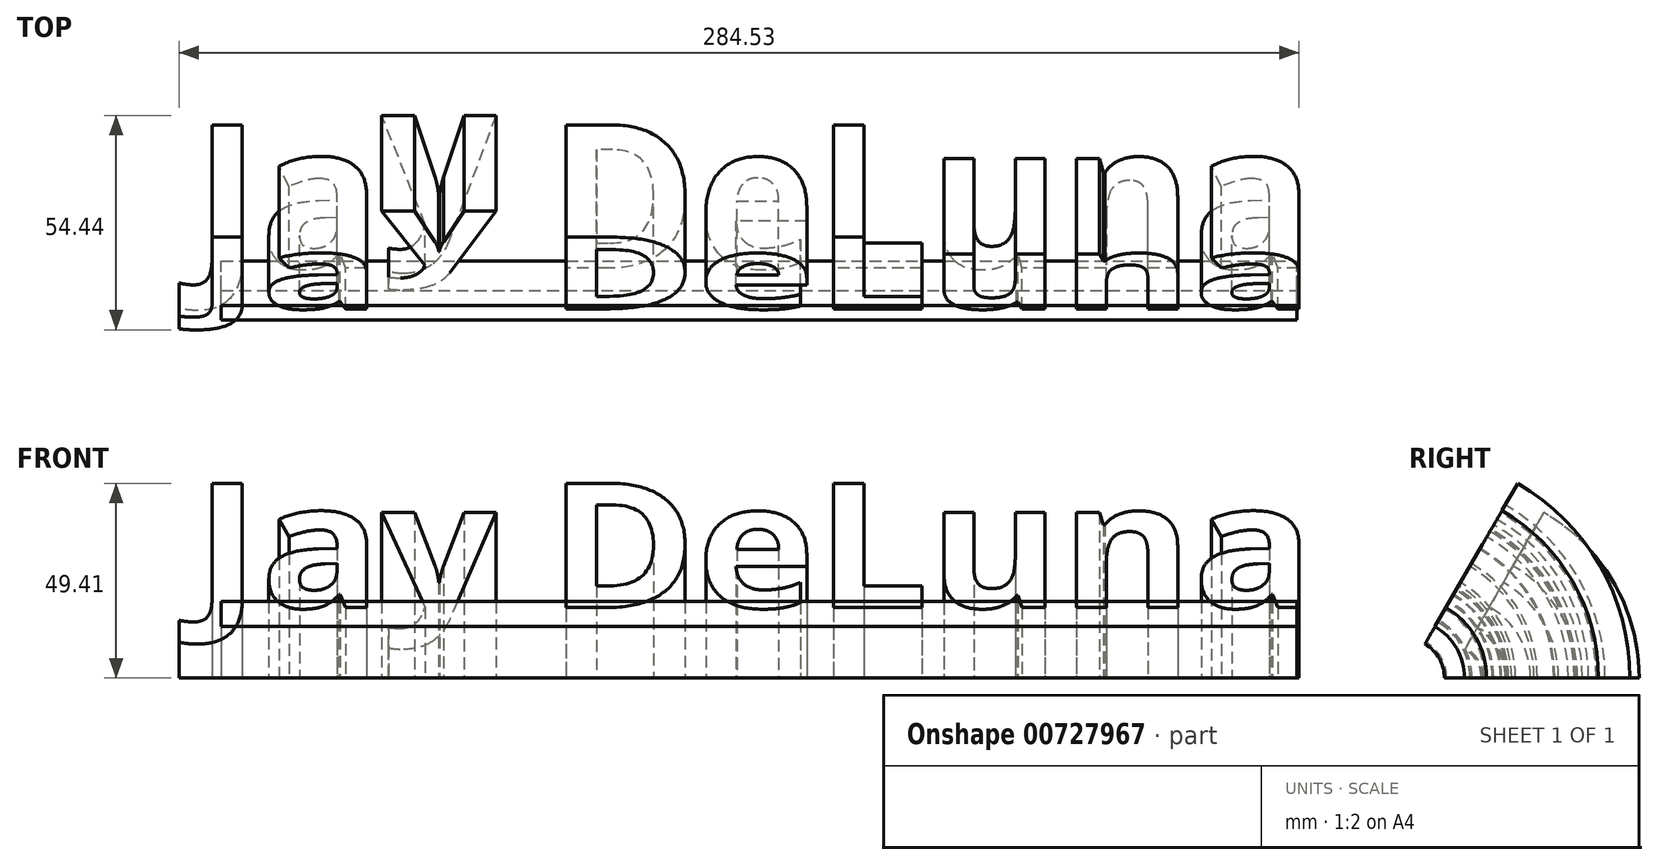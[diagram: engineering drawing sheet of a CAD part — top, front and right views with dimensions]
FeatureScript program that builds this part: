
annotation { "Feature Type Name" : "Feature", "Feature Type Description" : "" }
export const myFeature = defineFeature(function(context is Context, id is Id, definition is map)
    precondition{}
    {
        {
            var Q0;
            Q0=qCreatedBy(makeId("Top.planeOp"),FACE);
            var sketch = newSketch(context, id + "F0", { "sketchPlane" : qUnion([Q0])});
            skText(sketch, "E0", { "text": "Jay DeLuna", "fontName": "OpenSans-Bold.ttf"});
            const initialGuessF0  = {"E0": [-0.11567, -0.01428, 1, 0, 0.03673]};
            skSetInitialGuess(sketch, initialGuessF0);
            skSolve(sketch);
        }
        {
            var Q0;
            Q0=qCreatedBy(makeId("Top.planeOp"),FACE);
            var sketch = newSketch(context, id + "F1", { "sketchPlane" : qUnion([Q0])});
            skLineSegment(sketch, "E1", {"start": v(-125.24, -34.91) * mm, "end": v(145.49, -34.91) * mm});
            skSolve(sketch);
        }
        {
            var Q0;
            Q0=qCreatedBy(makeId("Top.planeOp"),FACE);
            var sketch = newSketch(context, id + "F2", { "sketchPlane" : qUnion([Q0])});
            skLineSegment(sketch, "E2.bottom", {"start": v(-108.77, -19.88) * mm, "end": v(164.57, -19.88) * mm});
            skLineSegment(sketch, "E2.top", {"start": v(-108.77, -12.48) * mm, "end": v(164.57, -12.48) * mm});
            skLineSegment(sketch, "E2.left", {"start": v(-108.77, -19.88) * mm, "end": v(-108.77, -12.48) * mm});
            skLineSegment(sketch, "E2.right", {"start": v(164.57, -19.88) * mm, "end": v(164.57, -12.48) * mm});
            skSolve(sketch);
        }
        {
            var Q0;
            Q0 = qSketchRegion(id + "F0", true);
            var Q1;
            Q1=makeQuery(id+"F2.imprint","IMPRINT",FACE,{"disambiguationData":[TD([[makeQuery(id+"F2.imprint","IMPRINT",EDGE,{"derivedFrom":sQuery(id+"F2.wireOp",EDGE,"E2.bottom")}),1.0]])]});
            var Q2;
            Q2=sQuery(id+"F1.wireOp",EDGE,"E1");
            revolve(context, id + "F3", {"surfaceOperationType" : NewSurfaceOperationType.NEW, "entities" : qUnion([Q0, Q1]), "axis" : qUnion([Q2]), "revolveType" : RevolveType.ONE_DIRECTION, "angle" : 60 * degree});
        }
        {
            var Q0;
            Q0=makeQuery(id+"F3.opRevolve","SWEPT_BODY",BODY,{"disambiguationData":[OSD([sQuery(id+"F0.wireOp",EDGE,"E0.sketch_text.stroke-35"),sQuery(id+"F0.wireOp",EDGE,"E0.sketch_text.stroke-36"),sQuery(id+"F0.wireOp",EDGE,"E0.sketch_text.stroke-37"),sQuery(id+"F0.wireOp",EDGE,"E0.sketch_text.stroke-38"),sQuery(id+"F0.wireOp",EDGE,"E0.sketch_text.stroke-39"),sQuery(id+"F0.wireOp",EDGE,"E0.sketch_text.stroke-40"),sQuery(id+"F0.wireOp",EDGE,"E0.sketch_text.stroke-41"),sQuery(id+"F0.wireOp",EDGE,"E0.sketch_text.stroke-42"),sQuery(id+"F0.wireOp",EDGE,"E0.sketch_text.stroke-43"),sQuery(id+"F0.wireOp",EDGE,"E0.sketch_text.stroke-44"),sQuery(id+"F0.wireOp",EDGE,"E0.sketch_text.stroke-45"),sQuery(id+"F0.wireOp",EDGE,"E0.sketch_text.stroke-46"),sQuery(id+"F0.wireOp",EDGE,"E0.sketch_text.stroke-47"),sQuery(id+"F0.wireOp",EDGE,"E0.sketch_text.stroke-48"),sQuery(id+"F0.wireOp",EDGE,"E0.sketch_text.stroke-49"),sQuery(id+"F0.wireOp",EDGE,"E0.sketch_text.stroke-50"),sQuery(id+"F0.wireOp",EDGE,"E0.sketch_text.stroke-51")])]});
            var Q1;
            Q1=qCreatedBy(makeId("Front.planeOp"),FACE);
            transform(context, id + "F4", {"entities" : qUnion([Q0]), "transformType" : TransformType.TRANSLATION_DISTANCE, "transformDirection" : qUnion([Q1]), "distance" : 10.92 * mm, "oppositeDirection" : true, "makeCopy" : false});
        }
    });
